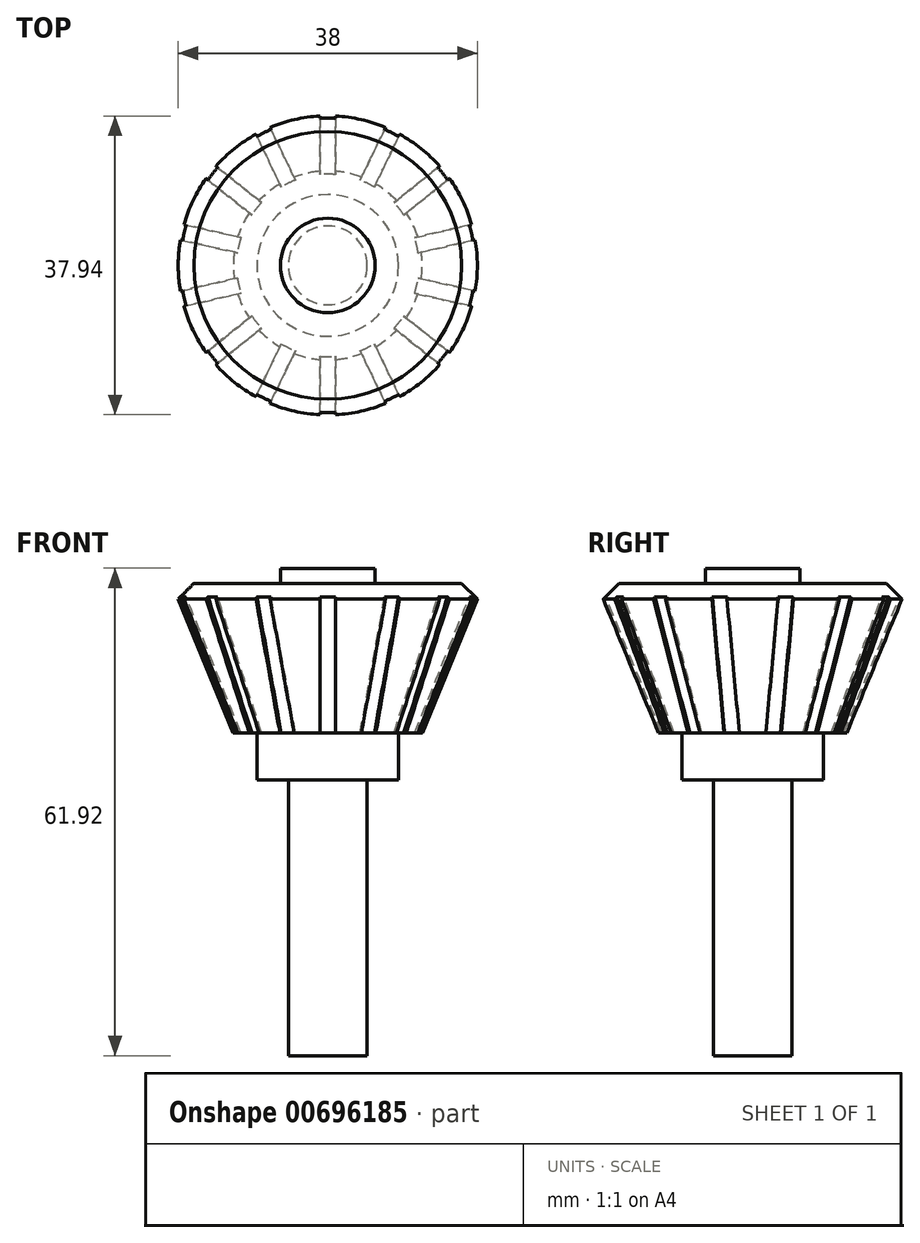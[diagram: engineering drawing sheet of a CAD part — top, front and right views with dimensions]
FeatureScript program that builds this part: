
annotation { "Feature Type Name" : "Feature", "Feature Type Description" : "" }
export const myFeature = defineFeature(function(context is Context, id is Id, definition is map)
    precondition{}
    {
        {
            var Q0;
            Q0=qCreatedBy(makeId("Front.planeOp"),FACE);
            var sketch = newSketch(context, id + "F0", { "sketchPlane" : qUnion([Q0])});
            skLineSegment(sketch, "E0", {"start": v(0, -3.04) * mm, "end": v(0, 2.5) * mm, "construction": true});
            skLineSegment(sketch, "E1", {"start": v(0, 0) * mm, "end": v(5, 0) * mm});
            skLineSegment(sketch, "E2", {"start": v(5, 0) * mm, "end": v(5, 35) * mm});
            skLineSegment(sketch, "E3", {"start": v(5, 35) * mm, "end": v(9, 35) * mm});
            skLineSegment(sketch, "E4", {"start": v(9, 35) * mm, "end": v(9, 41) * mm});
            skLineSegment(sketch, "E5", {"start": v(9, 41) * mm, "end": v(12, 41) * mm});
            skLineSegment(sketch, "E6", {"start": v(12, 41) * mm, "end": v(19, 58) * mm});
            skLineSegment(sketch, "E7", {"start": v(19, 58) * mm, "end": v(17, 60) * mm});
            skLineSegment(sketch, "E8", {"start": v(17, 60) * mm, "end": v(6, 60) * mm});
            skLineSegment(sketch, "E9", {"start": v(0, 60) * mm, "end": v(0, 0) * mm});
            skLineSegment(sketch, "E10", {"start": v(0, 60) * mm, "end": v(0, 61.92) * mm});
            skLineSegment(sketch, "E11", {"start": v(0, 61.92) * mm, "end": v(6, 61.92) * mm});
            skLineSegment(sketch, "E12", {"start": v(6, 61.92) * mm, "end": v(6, 60) * mm});
            skSolve(sketch);
        }
        {
            var Q0;
            Q0=makeQuery(id+"F0.imprint","IMPRINT",FACE,{"disambiguationData":[TD([[makeQuery(id+"F0.imprint","IMPRINT",EDGE,{"derivedFrom":sQuery(id+"F0.wireOp",EDGE,"E1")}),1.0]])]});
            var Q1;
            Q1 = qSketchRegion(id + "FC6jt78Kc8opL9K_1", true);
            var Q2;
            Q2=sQuery(id+"F0.wireOp",EDGE,"E0");
            revolve(context, id + "F1", {"surfaceOperationType" : NewSurfaceOperationType.NEW, "entities" : qUnion([Q0, Q1]), "axis" : qUnion([Q2]), "revolveType" : RevolveType.FULL});
        }
        {
            var Q0;
            Q0=makeQuery(id+"F1.opRevolve","SWEPT_FACE",FACE,{"disambiguationData":[OSD([sQuery(id+"F0.wireOp",EDGE,"E1")])]});
            var sketch = newSketch(context, id + "F2", { "sketchPlane" : qUnion([Q0])});
            skLineSegment(sketch, "E13.bottom", {"start": v(-1, 20) * mm, "end": v(1, 20) * mm});
            skLineSegment(sketch, "E13.left", {"start": v(-1, 20) * mm, "end": v(-1, 11) * mm});
            skLineSegment(sketch, "E13.right", {"start": v(1, 20) * mm, "end": v(1, 11) * mm});
            skLineSegment(sketch, "E14", {"start": v(1, 11) * mm, "end": v(-1, 11) * mm});
            skLineSegment(sketch, "E15.1.0", {"start": v(-7.78, 18.45) * mm, "end": v(-3.87, 10.34) * mm});
            skLineSegment(sketch, "E15.1.1", {"start": v(-9.58, 17.59) * mm, "end": v(-7.78, 18.45) * mm});
            skLineSegment(sketch, "E15.1.2", {"start": v(-9.58, 17.59) * mm, "end": v(-5.67, 9.48) * mm});
            skLineSegment(sketch, "E15.1.3", {"start": v(-3.87, 10.34) * mm, "end": v(-5.67, 9.48) * mm});
            skLineSegment(sketch, "E15.2.0", {"start": v(-15.01, 13.25) * mm, "end": v(-7.98, 7.64) * mm});
            skLineSegment(sketch, "E15.2.1", {"start": v(-16.26, 11.69) * mm, "end": v(-15.01, 13.25) * mm});
            skLineSegment(sketch, "E15.2.2", {"start": v(-16.26, 11.69) * mm, "end": v(-9.22, 6.08) * mm});
            skLineSegment(sketch, "E15.2.3", {"start": v(-7.98, 7.64) * mm, "end": v(-9.22, 6.08) * mm});
            skLineSegment(sketch, "E15.3.0", {"start": v(-19.28, 5.43) * mm, "end": v(-10.5, 3.42) * mm});
            skLineSegment(sketch, "E15.3.1", {"start": v(-19.72, 3.48) * mm, "end": v(-19.28, 5.43) * mm});
            skLineSegment(sketch, "E15.3.2", {"start": v(-19.72, 3.48) * mm, "end": v(-10.95, 1.47) * mm});
            skLineSegment(sketch, "E15.3.3", {"start": v(-10.5, 3.42) * mm, "end": v(-10.95, 1.47) * mm});
            skLineSegment(sketch, "E15.4.0", {"start": v(-19.72, -3.48) * mm, "end": v(-10.95, -1.47) * mm});
            skLineSegment(sketch, "E15.4.1", {"start": v(-19.28, -5.43) * mm, "end": v(-19.72, -3.48) * mm});
            skLineSegment(sketch, "E15.4.2", {"start": v(-19.28, -5.43) * mm, "end": v(-10.5, -3.42) * mm});
            skLineSegment(sketch, "E15.4.3", {"start": v(-10.95, -1.47) * mm, "end": v(-10.5, -3.42) * mm});
            skLineSegment(sketch, "E15.5.0", {"start": v(-16.26, -11.69) * mm, "end": v(-9.22, -6.08) * mm});
            skLineSegment(sketch, "E15.5.1", {"start": v(-15.01, -13.25) * mm, "end": v(-16.26, -11.69) * mm});
            skLineSegment(sketch, "E15.5.2", {"start": v(-15.01, -13.25) * mm, "end": v(-7.98, -7.64) * mm});
            skLineSegment(sketch, "E15.5.3", {"start": v(-9.22, -6.08) * mm, "end": v(-7.98, -7.64) * mm});
            skLineSegment(sketch, "E15.6.0", {"start": v(-9.58, -17.59) * mm, "end": v(-5.67, -9.48) * mm});
            skLineSegment(sketch, "E15.6.1", {"start": v(-7.78, -18.45) * mm, "end": v(-9.58, -17.59) * mm});
            skLineSegment(sketch, "E15.6.2", {"start": v(-7.78, -18.45) * mm, "end": v(-3.87, -10.34) * mm});
            skLineSegment(sketch, "E15.6.3", {"start": v(-5.67, -9.48) * mm, "end": v(-3.87, -10.34) * mm});
            skLineSegment(sketch, "E15.7.0", {"start": v(-1, -20) * mm, "end": v(-1, -11) * mm});
            skLineSegment(sketch, "E15.7.1", {"start": v(1, -20) * mm, "end": v(-1, -20) * mm});
            skLineSegment(sketch, "E15.7.2", {"start": v(1, -20) * mm, "end": v(1, -11) * mm});
            skLineSegment(sketch, "E15.7.3", {"start": v(-1, -11) * mm, "end": v(1, -11) * mm});
            skLineSegment(sketch, "E15.8.0", {"start": v(7.78, -18.45) * mm, "end": v(3.87, -10.34) * mm});
            skLineSegment(sketch, "E15.8.1", {"start": v(9.58, -17.59) * mm, "end": v(7.78, -18.45) * mm});
            skLineSegment(sketch, "E15.8.2", {"start": v(9.58, -17.59) * mm, "end": v(5.67, -9.48) * mm});
            skLineSegment(sketch, "E15.8.3", {"start": v(3.87, -10.34) * mm, "end": v(5.67, -9.48) * mm});
            skLineSegment(sketch, "E15.9.0", {"start": v(15.01, -13.25) * mm, "end": v(7.98, -7.64) * mm});
            skLineSegment(sketch, "E15.9.1", {"start": v(16.26, -11.69) * mm, "end": v(15.01, -13.25) * mm});
            skLineSegment(sketch, "E15.9.2", {"start": v(16.26, -11.69) * mm, "end": v(9.22, -6.08) * mm});
            skLineSegment(sketch, "E15.9.3", {"start": v(7.98, -7.64) * mm, "end": v(9.22, -6.08) * mm});
            skPoint(sketch, "E15.center", {"position": v(0, 0) * mm});
            skLineSegment(sketch, "E16.2.10.0", {"start": v(19.28, -5.43) * mm, "end": v(10.5, -3.42) * mm});
            skLineSegment(sketch, "E16.3.10.0", {"start": v(19.72, -3.48) * mm, "end": v(19.28, -5.43) * mm});
            skLineSegment(sketch, "E16.6.10.0", {"start": v(19.72, -3.48) * mm, "end": v(10.95, -1.47) * mm});
            skLineSegment(sketch, "E16.9.10.0", {"start": v(10.5, -3.42) * mm, "end": v(10.95, -1.47) * mm});
            skLineSegment(sketch, "E17.2.11.0", {"start": v(19.72, 3.48) * mm, "end": v(10.95, 1.47) * mm});
            skLineSegment(sketch, "E17.3.11.0", {"start": v(19.28, 5.43) * mm, "end": v(19.72, 3.48) * mm});
            skLineSegment(sketch, "E17.6.11.0", {"start": v(19.28, 5.43) * mm, "end": v(10.5, 3.42) * mm});
            skLineSegment(sketch, "E17.9.11.0", {"start": v(10.95, 1.47) * mm, "end": v(10.5, 3.42) * mm});
            skLineSegment(sketch, "E18.2.12.0", {"start": v(16.26, 11.69) * mm, "end": v(9.22, 6.08) * mm});
            skLineSegment(sketch, "E18.3.12.0", {"start": v(15.01, 13.25) * mm, "end": v(16.26, 11.69) * mm});
            skLineSegment(sketch, "E18.6.12.0", {"start": v(15.01, 13.25) * mm, "end": v(7.98, 7.64) * mm});
            skLineSegment(sketch, "E18.9.12.0", {"start": v(9.22, 6.08) * mm, "end": v(7.98, 7.64) * mm});
            skLineSegment(sketch, "E18.2.13.0", {"start": v(9.58, 17.59) * mm, "end": v(5.67, 9.48) * mm});
            skLineSegment(sketch, "E18.3.13.0", {"start": v(7.78, 18.45) * mm, "end": v(9.58, 17.59) * mm});
            skLineSegment(sketch, "E18.6.13.0", {"start": v(7.78, 18.45) * mm, "end": v(3.87, 10.34) * mm});
            skLineSegment(sketch, "E18.9.13.0", {"start": v(5.67, 9.48) * mm, "end": v(3.87, 10.34) * mm});
            skSolve(sketch);
        }
        {
            var Q0;
            Q0 = qSketchRegion(id + "F2", true);
            var Q1;
            Q1=makeQuery(id+"F1.opRevolve","SWEPT_FACE",FACE,{"disambiguationData":[OSD([sQuery(id+"F0.wireOp",EDGE,"E6")])]});
            extrude(context, id + "F3", {"entities" : qUnion([Q0]), "operationType" : NewBodyOperationType.REMOVE, "endBound" : BoundingType.UP_TO_SURFACE, "oppositeDirection" : true, "depth" : 25 * mm, "endBoundEntityFace" : qUnion([Q1]), "hasOffset" : true, "offsetDistance" : 1 * mm, "offsetOppositeDirection" : true});
        }
    });
